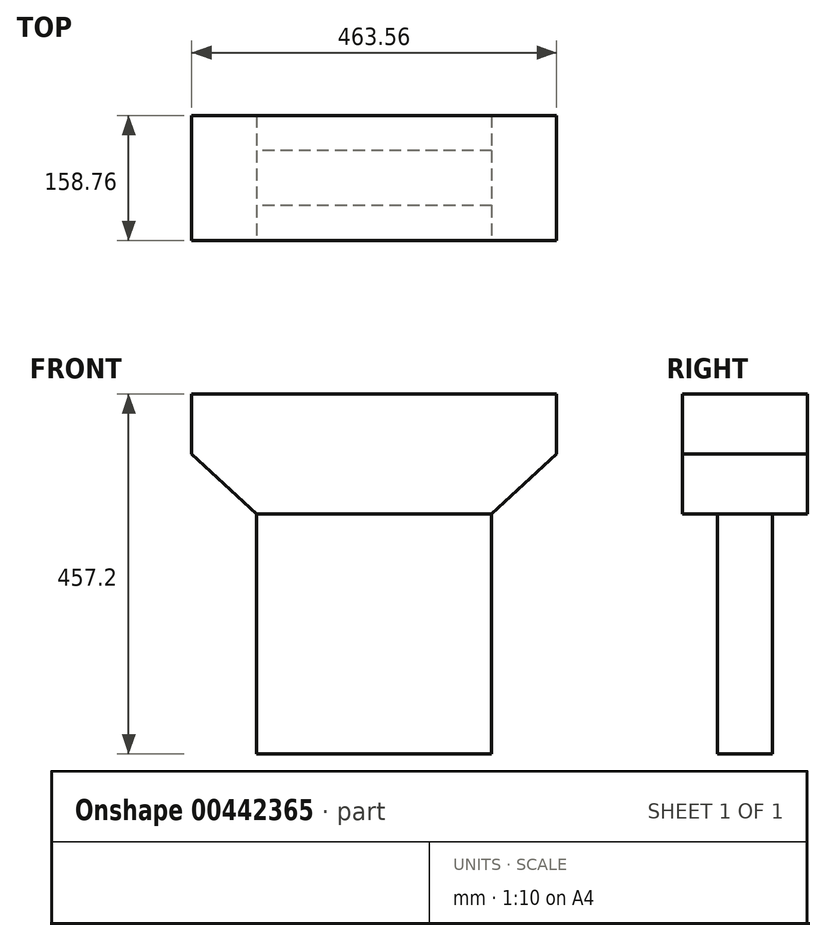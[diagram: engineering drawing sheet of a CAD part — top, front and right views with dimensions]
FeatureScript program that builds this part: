
annotation { "Feature Type Name" : "Feature", "Feature Type Description" : "" }
export const myFeature = defineFeature(function(context is Context, id is Id, definition is map)
    precondition{}
    {
        {
            var Q0;
            Q0=qCreatedBy(makeId("Top.planeOp"),FACE);
            var sketch = newSketch(context, id + "F0", { "sketchPlane" : qUnion([Q0])});
            skLineSegment(sketch, "E0.bottom", {"start": v(-231.78, 79.38) * mm, "end": v(231.78, 79.38) * mm});
            skLineSegment(sketch, "E0.top", {"start": v(-231.78, -79.37) * mm, "end": v(231.77, -79.37) * mm});
            skLineSegment(sketch, "E0.left", {"start": v(-231.77, 79.38) * mm, "end": v(-231.78, -79.37) * mm});
            skLineSegment(sketch, "E0.right", {"start": v(231.78, 79.38) * mm, "end": v(231.77, -79.37) * mm});
            skPoint(sketch, "E0.middle", {"position": v(0, 0) * mm});
            skSolve(sketch);
        }
        {
            var Q0;
            Q0=makeQuery(id+"F0.imprint","IMPRINT",FACE,{"disambiguationData":[TD([[makeQuery(id+"F0.imprint","IMPRINT",EDGE,{"derivedFrom":sQuery(id+"F0.wireOp",EDGE,"E0.bottom")}),-1.0]])]});
            extrude(context, id + "F1", {"entities" : qUnion([Q0]), "depth" : 457.2 * mm});
        }
        {
            var Q0;
            Q0=makeQuery(id+"F1.opExtrude","SWEPT_FACE",FACE,{"disambiguationData":[OSD([sQuery(id+"F0.wireOp",EDGE,"E0.top")])]});
            var sketch = newSketch(context, id + "F2", { "sketchPlane" : qUnion([Q0])});
            skLineSegment(sketch, "E1", {"start": v(-149.23, 304.8) * mm, "end": v(-149.22, 0) * mm});
            skLineSegment(sketch, "E2", {"start": v(0, 457.2) * mm, "end": v(0, 0) * mm});
            skLineSegment(sketch, "E3", {"start": v(-231.78, 457.2) * mm, "end": v(-231.78, 381) * mm});
            skLineSegment(sketch, "E4", {"start": v(-231.78, 381) * mm, "end": v(-149.22, 304.8) * mm});
            skLineSegment(sketch, "E5.MirrorCS", {"start": v(149.23, 304.8) * mm, "end": v(149.23, 0) * mm});
            skLineSegment(sketch, "E6.MirrorCS", {"start": v(231.78, 381) * mm, "end": v(149.22, 304.8) * mm});
            skLineSegment(sketch, "E7.MirrorCS", {"start": v(231.77, 457.2) * mm, "end": v(231.77, 381) * mm});
            skLineSegment(sketch, "E8", {"start": v(-231.78, 381) * mm, "end": v(-231.78, 0) * mm});
            skLineSegment(sketch, "E9", {"start": v(-231.78, 0) * mm, "end": v(-149.22, 0) * mm});
            skLineSegment(sketch, "E10", {"start": v(231.78, 381) * mm, "end": v(231.78, 0) * mm});
            skLineSegment(sketch, "E11", {"start": v(231.77, 0) * mm, "end": v(149.23, 0) * mm});
            skSolve(sketch);
        }
        {
            var Q0;
            Q0=makeQuery(id+"F2.imprint","IMPRINT",FACE,{"disambiguationData":[TD([[makeQuery(id+"F2.imprint","IMPRINT",EDGE,{"derivedFrom":sQuery(id+"F2.wireOp",EDGE,"E1")}),-1.0]])]});
            var Q1;
            Q1=makeQuery(id+"F2.imprint","IMPRINT",FACE,{"disambiguationData":[TD([[makeQuery(id+"F2.imprint","IMPRINT",EDGE,{"derivedFrom":sQuery(id+"F2.wireOp",EDGE,"E5.MirrorCS")}),1.0]])]});
            extrude(context, id + "F3", {"entities" : qUnion([Q0, Q1]), "operationType" : NewBodyOperationType.REMOVE, "endBound" : BoundingType.THROUGH_ALL, "oppositeDirection" : true, "depth" : 25.4 * mm});
        }
        {
            var Q0;
            Q0=makeQuery(id+"F3.boolean.opBoolean","COPY",FACE,{"derivedFrom":makeQuery(id+"F3.opExtrude","SWEPT_FACE",FACE,{"disambiguationData":[OSD([sQuery(id+"F2.wireOp",EDGE,"E1")])]})});
            var sketch = newSketch(context, id + "F4", { "sketchPlane" : qUnion([Q0])});
            skLineSegment(sketch, "E12", {"start": v(-34.93, 0) * mm, "end": v(-34.93, 304.8) * mm});
            skLineSegment(sketch, "E13.MirrorCS", {"start": v(34.93, 0) * mm, "end": v(34.93, 304.8) * mm});
            skLineSegment(sketch, "E14", {"start": v(-34.93, 304.8) * mm, "end": v(-79.38, 304.8) * mm});
            skLineSegment(sketch, "E15", {"start": v(-79.38, 304.8) * mm, "end": v(-79.38, 0) * mm});
            skLineSegment(sketch, "E16", {"start": v(-79.38, 0) * mm, "end": v(-34.93, 0) * mm});
            skLineSegment(sketch, "E17", {"start": v(34.93, 304.8) * mm, "end": v(79.37, 304.8) * mm});
            skLineSegment(sketch, "E18", {"start": v(79.37, 304.8) * mm, "end": v(79.37, 0) * mm});
            skLineSegment(sketch, "E19", {"start": v(79.37, 0) * mm, "end": v(34.93, 0) * mm});
            skPoint(sketch, "E20.end.orphan", {"position": v(0, 304.8) * mm});
            skSolve(sketch);
        }
        {
            var Q0;
            Q0=makeQuery(id+"F4.imprint","IMPRINT",FACE,{"disambiguationData":[TD([[makeQuery(id+"F4.imprint","IMPRINT",EDGE,{"derivedFrom":sQuery(id+"F4.wireOp",EDGE,"E12")}),1.0]])]});
            var Q1;
            Q1=makeQuery(id+"F4.imprint","IMPRINT",FACE,{"disambiguationData":[TD([[makeQuery(id+"F4.imprint","IMPRINT",EDGE,{"derivedFrom":sQuery(id+"F4.wireOp",EDGE,"E13.MirrorCS")}),-1.0]])]});
            extrude(context, id + "F5", {"entities" : qUnion([Q0, Q1]), "operationType" : NewBodyOperationType.REMOVE, "endBound" : BoundingType.THROUGH_ALL, "oppositeDirection" : true, "depth" : 25.4 * mm});
        }
    });
